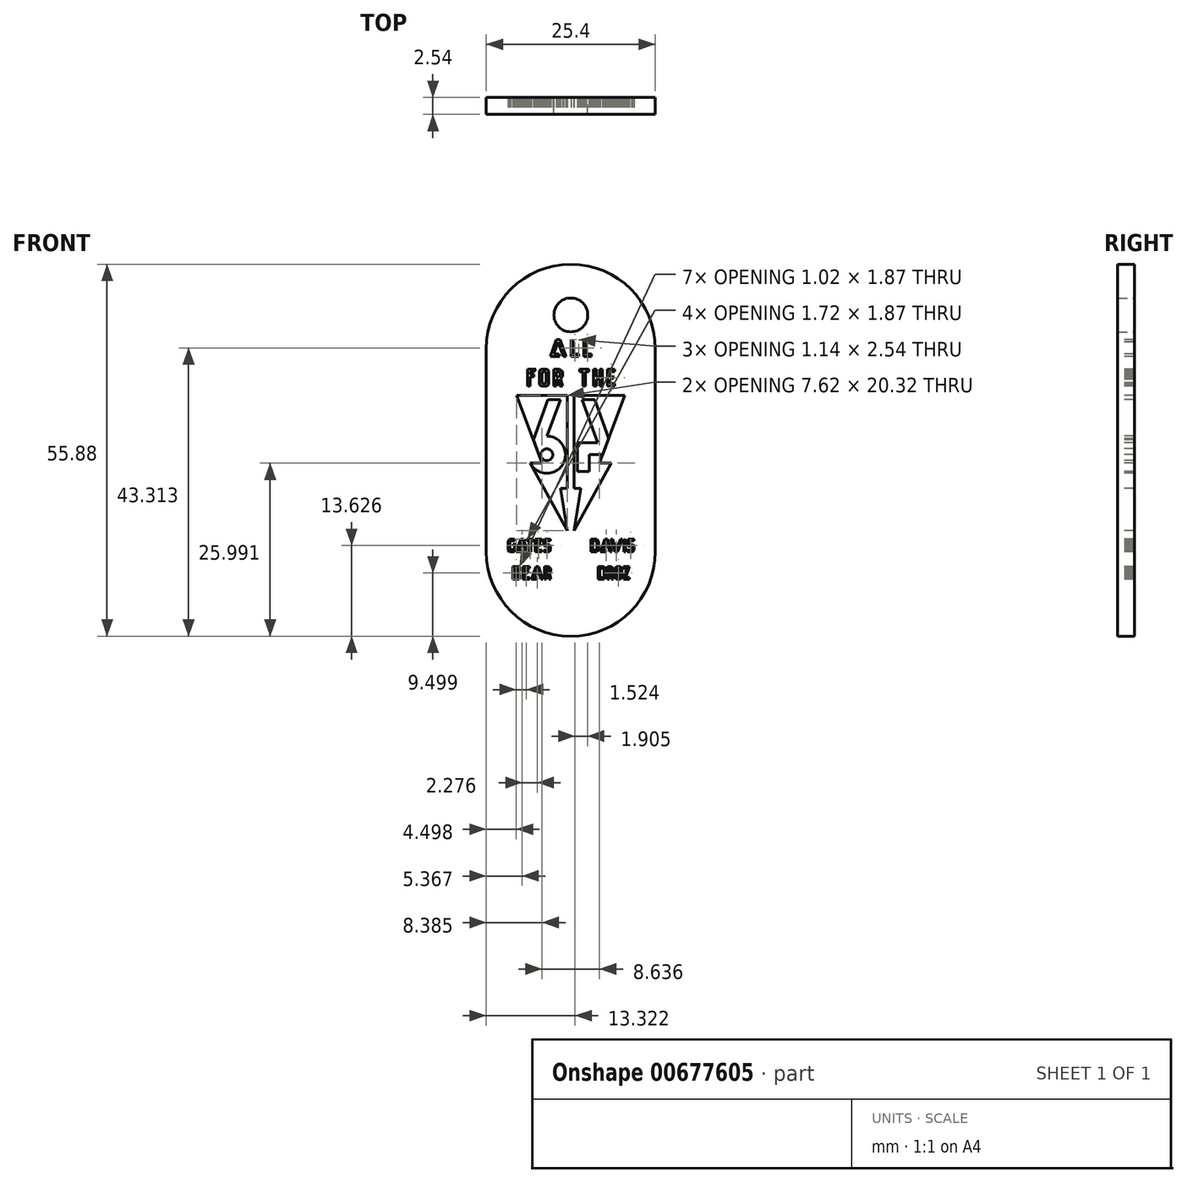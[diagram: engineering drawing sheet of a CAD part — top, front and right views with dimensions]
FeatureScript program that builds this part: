
annotation { "Feature Type Name" : "Feature", "Feature Type Description" : "" }
export const myFeature = defineFeature(function(context is Context, id is Id, definition is map)
    precondition{}
    {
        {
            var Q0;
            Q0=qCreatedBy(makeId("Front.planeOp"),FACE);
            var sketch = newSketch(context, id + "F0", { "sketchPlane" : qUnion([Q0])});
            skLineSegment(sketch, "E0.bottom", {"start": v(-15.5, -1.83) * mm, "end": v(9.9, -1.83) * mm});
            skLineSegment(sketch, "E0.top", {"start": v(-15.5, -32.3) * mm, "end": v(9.9, -32.3) * mm});
            skLineSegment(sketch, "E0.left", {"start": v(-15.5, -1.83) * mm, "end": v(-15.5, -32.3) * mm});
            skLineSegment(sketch, "E0.right", {"start": v(9.9, -1.83) * mm, "end": v(9.9, -32.3) * mm});
            skArc(sketch, "E1", {"start": v(9.9, -1.83) * mm, "mid": v(-2.8, 10.87) * mm, "end": v(-15.5, -1.83) * mm});
            skArc(sketch, "E2", {"start": v(-15.5, -32.3) * mm, "mid": v(-2.8, -45) * mm, "end": v(9.9, -32.3) * mm});
            skCircle(sketch, "E3", {"center": v(-2.8, 3.25) * mm, "radius": 2.54 * mm});
            skSolve(sketch);
        }
        {
            var Q0;
            Q0=makeQuery(id+"F0.imprint","IMPRINT",FACE,{"disambiguationData":[TD([[makeQuery(id+"F0.imprint","IMPRINT",EDGE,{"derivedFrom":sQuery(id+"F0.wireOp",EDGE,"E0.bottom")}),1.0]])]});
            var Q1;
            Q1=makeQuery(id+"F0.imprint","IMPRINT",FACE,{"disambiguationData":[TD([[makeQuery(id+"F0.imprint","IMPRINT",EDGE,{"derivedFrom":sQuery(id+"F0.wireOp",EDGE,"E0.bottom")}),-1.0]])]});
            var Q2;
            Q2=makeQuery(id+"F0.imprint","IMPRINT",FACE,{"disambiguationData":[TD([[makeQuery(id+"F0.imprint","IMPRINT",EDGE,{"derivedFrom":sQuery(id+"F0.wireOp",EDGE,"E0.top")}),-1.0]])]});
            extrude(context, id + "F1", {"entities" : qUnion([Q0, Q1, Q2]), "depth" : 2.54 * mm, "offsetDistance" : 25.4 * mm});
        }
        {
            var Q0;
            Q0=makeQuery(id+"F1.opExtrude","CAP_FACE",FACE,{"disambiguationData":[OSD([sQuery(id+"F0.wireOp",EDGE,"E0.left"),sQuery(id+"F0.wireOp",EDGE,"E0.right"),sQuery(id+"F0.wireOp",EDGE,"E1"),sQuery(id+"F0.wireOp",EDGE,"E2"),sQuery(id+"F0.wireOp",EDGE,"E3")])],"isStart":false});
            var sketch = newSketch(context, id + "F2", { "sketchPlane" : qUnion([Q0])});
            skLineSegment(sketch, "E4", {"start": v(-3.3, -22.83) * mm, "end": v(-4.32, -22.83) * mm});
            skLineSegment(sketch, "E5", {"start": v(-4.32, -22.83) * mm, "end": v(-3.3, -29.18) * mm});
            skLineSegment(sketch, "E6", {"start": v(-3.3, -29.18) * mm, "end": v(-8.9, -19.02) * mm});
            skLineSegment(sketch, "E7", {"start": v(-8.9, -19.02) * mm, "end": v(-7.12, -19.02) * mm});
            skLineSegment(sketch, "E8", {"start": v(-7.12, -19.02) * mm, "end": v(-10.93, -8.86) * mm});
            skLineSegment(sketch, "E9", {"start": v(-10.93, -8.86) * mm, "end": v(-3.3, -8.86) * mm});
            skLineSegment(sketch, "E10", {"start": v(-3.3, -8.86) * mm, "end": v(-3.3, -22.83) * mm});
            skLineSegment(sketch, "E11", {"start": v(-2.8, -46) * mm, "end": v(-2.8, 11.72) * mm});
            skPoint(sketch, "E11.startSnap0", {"position": v(-2.8, -45) * mm});
            skPoint(sketch, "E11.endSnap0", {"position": v(-2.8, 10.87) * mm});
            skLineSegment(sketch, "E12.MirrorCS", {"start": v(-2.29, -8.86) * mm, "end": v(-2.29, -22.83) * mm});
            skLineSegment(sketch, "E13.MirrorCS", {"start": v(5.33, -8.86) * mm, "end": v(-2.29, -8.86) * mm});
            skLineSegment(sketch, "E14.MirrorCS", {"start": v(1.52, -19.02) * mm, "end": v(5.33, -8.86) * mm});
            skLineSegment(sketch, "E15.MirrorCS", {"start": v(3.3, -19.02) * mm, "end": v(1.52, -19.02) * mm});
            skLineSegment(sketch, "E16.MirrorCS", {"start": v(-2.29, -29.18) * mm, "end": v(3.3, -19.02) * mm});
            skLineSegment(sketch, "E17.MirrorCS", {"start": v(-1.27, -22.83) * mm, "end": v(-2.29, -29.18) * mm});
            skLineSegment(sketch, "E18.MirrorCS", {"start": v(-2.29, -22.83) * mm, "end": v(-1.27, -22.83) * mm});
            skSolve(sketch);
        }
        {
            var Q0;
            Q0=makeQuery(id+"F2.imprint","IMPRINT",FACE,{"disambiguationData":[TD([[makeQuery(id+"F2.imprint","IMPRINT",EDGE,{"derivedFrom":sQuery(id+"F2.wireOp",EDGE,"E4")}),-1.0]])]});
            var Q1;
            Q1=makeQuery(id+"F2.imprint","IMPRINT",FACE,{"disambiguationData":[TD([[makeQuery(id+"F2.imprint","IMPRINT",EDGE,{"derivedFrom":sQuery(id+"F2.wireOp",EDGE,"E12.MirrorCS")}),1.0]])]});
            extrude(context, id + "F3", {"entities" : qUnion([Q0, Q1]), "operationType" : NewBodyOperationType.REMOVE, "oppositeDirection" : true, "depth" : 25.4 * mm, "offsetDistance" : 25.4 * mm});
        }
        {
            var Q0;
            Q0=makeQuery(id+"F1.opExtrude","CAP_FACE",FACE,{"disambiguationData":[OSD([sQuery(id+"F0.wireOp",EDGE,"E0.left"),sQuery(id+"F0.wireOp",EDGE,"E0.right"),sQuery(id+"F0.wireOp",EDGE,"E1"),sQuery(id+"F0.wireOp",EDGE,"E2"),sQuery(id+"F0.wireOp",EDGE,"E3")])],"isStart":false});
            var sketch = newSketch(context, id + "F4", { "sketchPlane" : qUnion([Q0])});
            skLineSegment(sketch, "E19", {"start": v(-1.78, -20.29) * mm, "end": v(-1.78, -15.97) * mm});
            skLineSegment(sketch, "E20", {"start": v(-1.78, -15.97) * mm, "end": v(1.27, -15.97) * mm});
            skLineSegment(sketch, "E21", {"start": v(1.27, -15.97) * mm, "end": v(0.13, -12.85) * mm});
            skLineSegment(sketch, "E22", {"start": v(1.52, -11.47) * mm, "end": v(3.8, -17.75) * mm});
            skLineSegment(sketch, "E23", {"start": v(3.8, -17.75) * mm, "end": v(0, -17.75) * mm});
            skLineSegment(sketch, "E24", {"start": v(0, -17.75) * mm, "end": v(0, -20.29) * mm});
            skLineSegment(sketch, "E25", {"start": v(0, -20.29) * mm, "end": v(-1.78, -20.29) * mm});
            skLineSegment(sketch, "E26", {"start": v(0.13, -12.85) * mm, "end": v(-1.09, -9.5) * mm});
            skLineSegment(sketch, "E27", {"start": v(-1.09, -9.5) * mm, "end": v(0.8, -9.5) * mm});
            skLineSegment(sketch, "E28", {"start": v(0.8, -9.5) * mm, "end": v(1.52, -11.47) * mm});
            skCircle(sketch, "E29", {"center": v(-6.4, -17.75) * mm, "radius": 2.8 * mm});
            skLineSegment(sketch, "E30", {"start": v(-8.67, -16.1) * mm, "end": v(-6.26, -9.5) * mm});
            skLineSegment(sketch, "E31", {"start": v(-6.26, -9.5) * mm, "end": v(-4.37, -9.5) * mm});
            skLineSegment(sketch, "E32", {"start": v(-4.37, -9.5) * mm, "end": v(-6.35, -14.96) * mm});
            skCircle(sketch, "E33", {"center": v(-6.4, -17.75) * mm, "radius": 0.89 * mm});
            skSolve(sketch);
        }
        {
            var Q0;
            {var subQ1=sQuery(id+"F4.wireOp",EDGE,"E31");Q0=makeQuery(id+"F4.imprint","IMPRINT",FACE,{"disambiguationData":[TD([[makeQuery(id+"F4.imprint","IMPRINT",EDGE,{"derivedFrom":subQ1}),-1.0]])]});}
            var Q1;
            Q1=makeQuery(id+"F4.imprint","IMPRINT",FACE,{"disambiguationData":[TD([[makeQuery(id+"F4.imprint","IMPRINT",EDGE,{"derivedFrom":sQuery(id+"F4.wireOp",EDGE,"E33")}),-1.0]])]});
            var Q2;
            Q2=makeQuery(id+"F4.imprint","IMPRINT",FACE,{"disambiguationData":[TD([[makeQuery(id+"F4.imprint","IMPRINT",EDGE,{"derivedFrom":sQuery(id+"F4.wireOp",EDGE,"E19")}),-1.0]])]});
            extrude(context, id + "F5", {"entities" : qUnion([Q0, Q1, Q2]), "oppositeDirection" : true, "depth" : 2.54 * mm, "offsetDistance" : 25.4 * mm});
        }
        {
            var Q0;
            Q0=makeQuery(id+"F1.opExtrude","CAP_FACE",FACE,{"disambiguationData":[OSD([sQuery(id+"F0.wireOp",EDGE,"E0.left"),sQuery(id+"F0.wireOp",EDGE,"E0.right"),sQuery(id+"F0.wireOp",EDGE,"E1"),sQuery(id+"F0.wireOp",EDGE,"E2"),sQuery(id+"F0.wireOp",EDGE,"E3")])],"isStart":false});
            var sketch = newSketch(context, id + "F6", { "sketchPlane" : qUnion([Q0])});
            skLineSegment(sketch, "E34", {"start": v(-5.9, -2.97) * mm, "end": v(-4.97, -0.43) * mm});
            skLineSegment(sketch, "E35", {"start": v(-4.97, -0.43) * mm, "end": v(-4.44, -0.43) * mm});
            skLineSegment(sketch, "E36", {"start": v(-4.44, -0.43) * mm, "end": v(-3.51, -2.97) * mm});
            skLineSegment(sketch, "E37", {"start": v(-3.51, -2.97) * mm, "end": v(-3.92, -2.97) * mm});
            skLineSegment(sketch, "E38", {"start": v(-3.92, -2.97) * mm, "end": v(-4.7, -0.8) * mm});
            skLineSegment(sketch, "E39", {"start": v(-4.7, -0.8) * mm, "end": v(-5.35, -2.59) * mm});
            skLineSegment(sketch, "E40", {"start": v(-5.35, -2.59) * mm, "end": v(-4.6, -2.59) * mm});
            skLineSegment(sketch, "E41", {"start": v(-4.6, -2.59) * mm, "end": v(-4.46, -2.97) * mm});
            skLineSegment(sketch, "E42", {"start": v(-4.46, -2.97) * mm, "end": v(-5.9, -2.97) * mm});
            skLineSegment(sketch, "E43", {"start": v(-2.75, -0.43) * mm, "end": v(-2.75, -2.97) * mm});
            skLineSegment(sketch, "E44", {"start": v(-2.75, -2.97) * mm, "end": v(-1.6, -2.97) * mm});
            skLineSegment(sketch, "E45", {"start": v(-1.6, -2.97) * mm, "end": v(-1.6, -2.59) * mm});
            skLineSegment(sketch, "E46", {"start": v(-1.6, -2.59) * mm, "end": v(-2.37, -2.59) * mm});
            skLineSegment(sketch, "E47", {"start": v(-2.37, -2.59) * mm, "end": v(-2.37, -0.75) * mm});
            skLineSegment(sketch, "E48", {"start": v(-2.37, -0.75) * mm, "end": v(-2.75, -0.43) * mm});
            skLineSegment(sketch, "E49", {"start": v(-0.84, -0.43) * mm, "end": v(-0.84, -2.97) * mm});
            skLineSegment(sketch, "E50", {"start": v(-0.84, -2.97) * mm, "end": v(0.3, -2.97) * mm});
            skLineSegment(sketch, "E51", {"start": v(0.3, -2.97) * mm, "end": v(0.3, -2.59) * mm});
            skLineSegment(sketch, "E52", {"start": v(0.3, -2.59) * mm, "end": v(-0.46, -2.59) * mm});
            skLineSegment(sketch, "E53", {"start": v(-0.46, -2.59) * mm, "end": v(-0.46, -0.75) * mm});
            skLineSegment(sketch, "E54", {"start": v(-0.46, -0.75) * mm, "end": v(-0.84, -0.43) * mm});
            skLineSegment(sketch, "E55", {"start": v(-9.28, -7.41) * mm, "end": v(-9.28, -4.87) * mm});
            skLineSegment(sketch, "E56", {"start": v(-9.28, -4.87) * mm, "end": v(-8.01, -4.87) * mm});
            skLineSegment(sketch, "E57", {"start": v(-8.01, -4.87) * mm, "end": v(-8.33, -5.25) * mm});
            skLineSegment(sketch, "E58", {"start": v(-8.33, -5.25) * mm, "end": v(-8.9, -5.25) * mm});
            skLineSegment(sketch, "E59", {"start": v(-8.9, -5.25) * mm, "end": v(-8.9, -5.63) * mm});
            skLineSegment(sketch, "E60", {"start": v(-8.9, -5.63) * mm, "end": v(-8.33, -5.63) * mm});
            skLineSegment(sketch, "E61", {"start": v(-8.33, -5.63) * mm, "end": v(-8.33, -6.01) * mm});
            skLineSegment(sketch, "E62", {"start": v(-8.33, -6.01) * mm, "end": v(-8.9, -6.01) * mm});
            skLineSegment(sketch, "E63", {"start": v(-8.9, -6.01) * mm, "end": v(-8.9, -7.41) * mm});
            skLineSegment(sketch, "E64", {"start": v(-8.9, -7.41) * mm, "end": v(-9.28, -7.41) * mm});
            skLineSegment(sketch, "E65", {"start": v(-7.25, -4.87) * mm, "end": v(-7.5, -5.13) * mm});
            skLineSegment(sketch, "E66", {"start": v(-7.5, -5.13) * mm, "end": v(-7.5, -7.16) * mm});
            skLineSegment(sketch, "E67", {"start": v(-7.5, -7.16) * mm, "end": v(-7.25, -7.41) * mm});
            skLineSegment(sketch, "E68", {"start": v(-7.25, -7.41) * mm, "end": v(-6.36, -7.41) * mm});
            skLineSegment(sketch, "E69", {"start": v(-6.36, -7.41) * mm, "end": v(-6.1, -7.16) * mm});
            skLineSegment(sketch, "E70", {"start": v(-6.1, -7.16) * mm, "end": v(-6.1, -5.13) * mm});
            skLineSegment(sketch, "E71", {"start": v(-6.1, -5.13) * mm, "end": v(-6.36, -4.87) * mm});
            skLineSegment(sketch, "E72", {"start": v(-6.36, -4.87) * mm, "end": v(-7.25, -4.87) * mm});
            skLineSegment(sketch, "E73", {"start": v(-5.34, -7.41) * mm, "end": v(-5.34, -4.87) * mm});
            skLineSegment(sketch, "E74", {"start": v(-5.34, -4.87) * mm, "end": v(-4.47, -4.87) * mm});
            skLineSegment(sketch, "E75", {"start": v(-4.47, -4.87) * mm, "end": v(-4.06, -5.29) * mm});
            skLineSegment(sketch, "E76", {"start": v(-4.06, -5.29) * mm, "end": v(-4.06, -5.98) * mm});
            skLineSegment(sketch, "E77", {"start": v(-4.06, -5.98) * mm, "end": v(-4.35, -6.27) * mm});
            skLineSegment(sketch, "E78", {"start": v(-4.35, -6.27) * mm, "end": v(-4.06, -7.41) * mm});
            skLineSegment(sketch, "E79", {"start": v(-4.06, -7.41) * mm, "end": v(-4.45, -7.41) * mm});
            skLineSegment(sketch, "E80", {"start": v(-4.45, -7.41) * mm, "end": v(-4.7, -6.4) * mm});
            skLineSegment(sketch, "E81", {"start": v(-4.7, -6.4) * mm, "end": v(-4.96, -6.4) * mm});
            skLineSegment(sketch, "E82", {"start": v(-4.96, -6.4) * mm, "end": v(-4.96, -7.41) * mm});
            skLineSegment(sketch, "E83", {"start": v(-4.96, -7.41) * mm, "end": v(-5.34, -7.41) * mm});
            skLineSegment(sketch, "E84", {"start": v(-7.12, -6.9) * mm, "end": v(-7, -7.03) * mm});
            skLineSegment(sketch, "E85", {"start": v(-7, -7.03) * mm, "end": v(-6.61, -7.03) * mm});
            skLineSegment(sketch, "E86", {"start": v(-6.61, -7.03) * mm, "end": v(-6.49, -6.9) * mm});
            skLineSegment(sketch, "E87", {"start": v(-6.49, -6.9) * mm, "end": v(-6.49, -5.38) * mm});
            skLineSegment(sketch, "E88", {"start": v(-6.49, -5.38) * mm, "end": v(-6.61, -5.25) * mm});
            skLineSegment(sketch, "E89", {"start": v(-6.61, -5.25) * mm, "end": v(-7, -5.25) * mm});
            skLineSegment(sketch, "E90", {"start": v(-7, -5.25) * mm, "end": v(-7.12, -5.38) * mm});
            skLineSegment(sketch, "E91", {"start": v(-7.12, -5.38) * mm, "end": v(-7.12, -6.9) * mm});
            skLineSegment(sketch, "E92", {"start": v(-4.96, -5.25) * mm, "end": v(-4.96, -6.01) * mm});
            skLineSegment(sketch, "E93", {"start": v(-4.96, -6.01) * mm, "end": v(-4.63, -6.01) * mm});
            skLineSegment(sketch, "E94", {"start": v(-4.63, -6.01) * mm, "end": v(-4.44, -5.82) * mm});
            skLineSegment(sketch, "E95", {"start": v(-4.44, -5.82) * mm, "end": v(-4.44, -5.44) * mm});
            skLineSegment(sketch, "E96", {"start": v(-4.44, -5.44) * mm, "end": v(-4.63, -5.25) * mm});
            skLineSegment(sketch, "E97", {"start": v(-4.63, -5.25) * mm, "end": v(-4.96, -5.25) * mm});
            skLineSegment(sketch, "E98", {"start": v(-1.52, -4.87) * mm, "end": v(-1.52, -5.25) * mm});
            skLineSegment(sketch, "E99", {"start": v(-1.52, -5.25) * mm, "end": v(-1.01, -5.25) * mm});
            skLineSegment(sketch, "E100", {"start": v(-1.01, -5.25) * mm, "end": v(-1.01, -7.41) * mm});
            skLineSegment(sketch, "E101", {"start": v(-1.01, -7.41) * mm, "end": v(-0.63, -7.41) * mm});
            skLineSegment(sketch, "E102", {"start": v(-0.63, -7.41) * mm, "end": v(-0.63, -5.25) * mm});
            skLineSegment(sketch, "E103", {"start": v(-0.63, -5.25) * mm, "end": v(-0.12, -5.25) * mm});
            skLineSegment(sketch, "E104", {"start": v(-0.12, -5.25) * mm, "end": v(-0.12, -4.87) * mm});
            skLineSegment(sketch, "E105", {"start": v(-1.52, -4.87) * mm, "end": v(-0.12, -4.87) * mm});
            skLineSegment(sketch, "E106", {"start": v(0.64, -4.87) * mm, "end": v(0.64, -7.41) * mm});
            skLineSegment(sketch, "E107", {"start": v(0.64, -7.41) * mm, "end": v(1.02, -7.41) * mm});
            skLineSegment(sketch, "E108", {"start": v(1.02, -7.41) * mm, "end": v(1.02, -6.4) * mm});
            skLineSegment(sketch, "E109", {"start": v(1.02, -6.4) * mm, "end": v(1.53, -6.4) * mm});
            skLineSegment(sketch, "E110", {"start": v(1.53, -6.4) * mm, "end": v(1.53, -7.41) * mm});
            skLineSegment(sketch, "E111", {"start": v(1.53, -7.41) * mm, "end": v(1.9, -7.41) * mm});
            skLineSegment(sketch, "E112", {"start": v(1.9, -7.41) * mm, "end": v(1.9, -4.87) * mm});
            skLineSegment(sketch, "E113", {"start": v(1.9, -4.87) * mm, "end": v(1.53, -4.87) * mm});
            skLineSegment(sketch, "E114", {"start": v(1.53, -4.87) * mm, "end": v(1.53, -6.01) * mm});
            skLineSegment(sketch, "E115", {"start": v(1.53, -6.01) * mm, "end": v(1.02, -6.01) * mm});
            skLineSegment(sketch, "E116", {"start": v(1.02, -6.01) * mm, "end": v(1.02, -4.87) * mm});
            skLineSegment(sketch, "E117", {"start": v(1.02, -4.87) * mm, "end": v(0.64, -4.87) * mm});
            skLineSegment(sketch, "E118", {"start": v(2.67, -4.87) * mm, "end": v(2.67, -7.41) * mm});
            skLineSegment(sketch, "E119", {"start": v(2.67, -7.41) * mm, "end": v(3.81, -7.41) * mm});
            skLineSegment(sketch, "E120", {"start": v(3.81, -7.41) * mm, "end": v(3.81, -7.03) * mm});
            skLineSegment(sketch, "E121", {"start": v(3.81, -7.03) * mm, "end": v(3.05, -7.03) * mm});
            skLineSegment(sketch, "E122", {"start": v(3.05, -7.03) * mm, "end": v(3.05, -6.4) * mm});
            skLineSegment(sketch, "E123", {"start": v(3.05, -6.4) * mm, "end": v(3.37, -6.4) * mm});
            skLineSegment(sketch, "E124", {"start": v(3.37, -6.4) * mm, "end": v(3.69, -6.01) * mm});
            skLineSegment(sketch, "E125", {"start": v(3.69, -6.01) * mm, "end": v(3.05, -6.01) * mm});
            skLineSegment(sketch, "E126", {"start": v(3.05, -6.01) * mm, "end": v(3.05, -5.25) * mm});
            skLineSegment(sketch, "E127", {"start": v(3.05, -5.25) * mm, "end": v(3.81, -5.25) * mm});
            skLineSegment(sketch, "E128", {"start": v(3.81, -5.25) * mm, "end": v(3.81, -4.87) * mm});
            skLineSegment(sketch, "E129", {"start": v(3.81, -4.87) * mm, "end": v(2.67, -4.87) * mm});
            skSolve(sketch);
        }
        {
            var Q0;
            Q0=makeQuery(id+"F6.imprint","IMPRINT",FACE,{"disambiguationData":[TD([[makeQuery(id+"F6.imprint","IMPRINT",EDGE,{"derivedFrom":sQuery(id+"F6.wireOp",EDGE,"E34")}),-1.0]])]});
            var Q1;
            Q1=makeQuery(id+"F6.imprint","IMPRINT",FACE,{"disambiguationData":[TD([[makeQuery(id+"F6.imprint","IMPRINT",EDGE,{"derivedFrom":sQuery(id+"F6.wireOp",EDGE,"E43")}),1.0]])]});
            var Q2;
            Q2=makeQuery(id+"F6.imprint","IMPRINT",FACE,{"disambiguationData":[TD([[makeQuery(id+"F6.imprint","IMPRINT",EDGE,{"derivedFrom":sQuery(id+"F6.wireOp",EDGE,"E49")}),1.0]])]});
            var Q3;
            Q3=makeQuery(id+"F6.imprint","IMPRINT",FACE,{"disambiguationData":[TD([[makeQuery(id+"F6.imprint","IMPRINT",EDGE,{"derivedFrom":sQuery(id+"F6.wireOp",EDGE,"9PJnOvU5-sTbl-nWi6-ZAvp-PHSVYoyPzlgs")}),-1.0]])]});
            var Q4;
            Q4=makeQuery(id+"F6.imprint","IMPRINT",FACE,{"disambiguationData":[TD([[makeQuery(id+"F6.imprint","IMPRINT",EDGE,{"derivedFrom":sQuery(id+"F6.wireOp",EDGE,"RmkwvY6V-nyv5-Yecy-RsY6-h2SH7d8XhEEe")}),-1.0]])]});
            var Q5;
            Q5=makeQuery(id+"F6.imprint","IMPRINT",FACE,{"disambiguationData":[TD([[makeQuery(id+"F6.imprint","IMPRINT",EDGE,{"derivedFrom":sQuery(id+"F6.wireOp",EDGE,"E55")}),-1.0]])]});
            var Q6;
            Q6=makeQuery(id+"F6.imprint","IMPRINT",FACE,{"disambiguationData":[TD([[makeQuery(id+"F6.imprint","IMPRINT",EDGE,{"derivedFrom":sQuery(id+"F6.wireOp",EDGE,"E65")}),1.0]])]});
            var Q7;
            Q7=makeQuery(id+"F6.imprint","IMPRINT",FACE,{"disambiguationData":[TD([[makeQuery(id+"F6.imprint","IMPRINT",EDGE,{"derivedFrom":sQuery(id+"F6.wireOp",EDGE,"E73")}),-1.0]])]});
            var Q8;
            Q8=makeQuery(id+"F6.imprint","IMPRINT",FACE,{"disambiguationData":[TD([[makeQuery(id+"F6.imprint","IMPRINT",EDGE,{"derivedFrom":sQuery(id+"F6.wireOp",EDGE,"E98")}),1.0]])]});
            var Q9;
            Q9=makeQuery(id+"F6.imprint","IMPRINT",FACE,{"disambiguationData":[TD([[makeQuery(id+"F6.imprint","IMPRINT",EDGE,{"derivedFrom":sQuery(id+"F6.wireOp",EDGE,"E106")}),1.0]])]});
            var Q10;
            Q10=makeQuery(id+"F6.imprint","IMPRINT",FACE,{"disambiguationData":[TD([[makeQuery(id+"F6.imprint","IMPRINT",EDGE,{"derivedFrom":sQuery(id+"F6.wireOp",EDGE,"E118")}),1.0]])]});
            extrude(context, id + "F7", {"entities" : qUnion([Q0, Q1, Q2, Q3, Q4, Q5, Q6, Q7, Q8, Q9, Q10]), "operationType" : NewBodyOperationType.REMOVE, "oppositeDirection" : true, "depth" : 25.4 * mm, "offsetDistance" : 25.4 * mm});
        }
        {
            var Q0;
            {var subQ0=sQuery(id+"F0.wireOp",EDGE,"E0.left");var subQ1=sQuery(id+"F0.wireOp",EDGE,"E1");var subQ2=sQuery(id+"F0.wireOp",EDGE,"E0.right");var subQ3=sQuery(id+"F0.wireOp",EDGE,"E2");var subQ4=sQuery(id+"F0.wireOp",EDGE,"E3");Q0=makeQuery(id+"F7.boolean.opBoolean","SPLIT",FACE,{"disambiguationData":[TD([makeQuery(id+"F1.opExtrude","SWEPT_FACE",FACE,{"disambiguationData":[OSD([subQ0])]})])],"derivedFrom":makeQuery(id+"F1.opExtrude","CAP_FACE",FACE,{"disambiguationData":[OSD([subQ0,subQ2,subQ1,subQ3,subQ4])],"isStart":false})});}
            var sketch = newSketch(context, id + "F8", { "sketchPlane" : qUnion([Q0])});
            skLineSegment(sketch, "E130", {"start": v(-12.2, -30.78) * mm, "end": v(-12.2, -31.99) * mm});
            skLineSegment(sketch, "E131", {"start": v(-12.2, -31.99) * mm, "end": v(-12, -32.32) * mm});
            skLineSegment(sketch, "E132", {"start": v(-12, -32.32) * mm, "end": v(-11.25, -32.32) * mm});
            skLineSegment(sketch, "E133", {"start": v(-11.25, -32.32) * mm, "end": v(-11.01, -31.91) * mm});
            skLineSegment(sketch, "E134", {"start": v(-11.01, -31.91) * mm, "end": v(-11.01, -31.21) * mm});
            skLineSegment(sketch, "E135", {"start": v(-11.01, -31.21) * mm, "end": v(-11.44, -31.21) * mm});
            skLineSegment(sketch, "E136", {"start": v(-11.44, -31.21) * mm, "end": v(-11.44, -31.46) * mm});
            skLineSegment(sketch, "E137", {"start": v(-11.44, -31.46) * mm, "end": v(-11.27, -31.46) * mm});
            skLineSegment(sketch, "E138", {"start": v(-11.27, -31.46) * mm, "end": v(-11.27, -31.85) * mm});
            skLineSegment(sketch, "E139", {"start": v(-11.27, -31.85) * mm, "end": v(-11.37, -32.02) * mm});
            skLineSegment(sketch, "E140", {"start": v(-11.37, -32.02) * mm, "end": v(-11.84, -32.02) * mm});
            skLineSegment(sketch, "E141", {"start": v(-11.84, -32.02) * mm, "end": v(-11.94, -31.85) * mm});
            skLineSegment(sketch, "E142", {"start": v(-11.94, -31.85) * mm, "end": v(-11.94, -30.88) * mm});
            skLineSegment(sketch, "E143", {"start": v(-11.94, -30.88) * mm, "end": v(-11.84, -30.7) * mm});
            skLineSegment(sketch, "E144", {"start": v(-11.84, -30.7) * mm, "end": v(-11.27, -30.7) * mm});
            skLineSegment(sketch, "E145", {"start": v(-11.27, -30.7) * mm, "end": v(-11.27, -30.45) * mm});
            skLineSegment(sketch, "E146", {"start": v(-11.27, -30.45) * mm, "end": v(-12, -30.45) * mm});
            skLineSegment(sketch, "E147", {"start": v(-12, -30.45) * mm, "end": v(-12.2, -30.78) * mm});
            skLineSegment(sketch, "E148", {"start": v(-11, -32.32) * mm, "end": v(-10.31, -30.45) * mm});
            skLineSegment(sketch, "E149", {"start": v(-9.95, -30.45) * mm, "end": v(-9.27, -32.32) * mm});
            skLineSegment(sketch, "E150", {"start": v(-9.27, -32.32) * mm, "end": v(-9.54, -32.32) * mm});
            skLineSegment(sketch, "E151", {"start": v(-9.54, -32.32) * mm, "end": v(-10.13, -30.7) * mm});
            skLineSegment(sketch, "E152", {"start": v(-10.13, -30.7) * mm, "end": v(-10.63, -32.06) * mm});
            skLineSegment(sketch, "E153", {"start": v(-10.63, -32.06) * mm, "end": v(-10.25, -32.06) * mm});
            skLineSegment(sketch, "E154", {"start": v(-10.25, -32.06) * mm, "end": v(-10.1, -32.32) * mm});
            skLineSegment(sketch, "E155", {"start": v(-10.1, -32.32) * mm, "end": v(-11, -32.32) * mm});
            skLineSegment(sketch, "E156", {"start": v(-10.31, -30.45) * mm, "end": v(-9.95, -30.45) * mm});
            skLineSegment(sketch, "E157", {"start": v(-9.4, -30.45) * mm, "end": v(-8.39, -30.45) * mm});
            skLineSegment(sketch, "E158", {"start": v(-8.39, -30.45) * mm, "end": v(-8.39, -30.7) * mm});
            skLineSegment(sketch, "E159", {"start": v(-8.39, -30.7) * mm, "end": v(-8.77, -30.7) * mm});
            skLineSegment(sketch, "E160", {"start": v(-8.77, -30.7) * mm, "end": v(-8.77, -32.32) * mm});
            skLineSegment(sketch, "E161", {"start": v(-8.77, -32.32) * mm, "end": v(-9.02, -32.32) * mm});
            skLineSegment(sketch, "E162", {"start": v(-9.02, -32.32) * mm, "end": v(-9.02, -30.7) * mm});
            skLineSegment(sketch, "E163", {"start": v(-9.02, -30.7) * mm, "end": v(-9.4, -30.7) * mm});
            skLineSegment(sketch, "E164", {"start": v(-9.4, -30.7) * mm, "end": v(-9.4, -30.45) * mm});
            skLineSegment(sketch, "E165", {"start": v(-8.13, -32.32) * mm, "end": v(-7.12, -32.32) * mm});
            skLineSegment(sketch, "E166", {"start": v(-7.12, -32.32) * mm, "end": v(-7.12, -32.06) * mm});
            skLineSegment(sketch, "E167", {"start": v(-7.12, -32.06) * mm, "end": v(-7.88, -32.06) * mm});
            skLineSegment(sketch, "E168", {"start": v(-7.88, -32.06) * mm, "end": v(-7.88, -31.4) * mm});
            skLineSegment(sketch, "E169", {"start": v(-7.88, -31.4) * mm, "end": v(-7.39, -31.4) * mm});
            skLineSegment(sketch, "E170", {"start": v(-7.39, -31.4) * mm, "end": v(-7.24, -31.15) * mm});
            skLineSegment(sketch, "E171", {"start": v(-7.24, -31.15) * mm, "end": v(-7.88, -31.15) * mm});
            skLineSegment(sketch, "E172", {"start": v(-7.12, -30.45) * mm, "end": v(-8.13, -30.45) * mm});
            skLineSegment(sketch, "E173", {"start": v(-5.85, -30.45) * mm, "end": v(-6.7, -30.45) * mm});
            skLineSegment(sketch, "E174", {"start": v(-6.7, -30.45) * mm, "end": v(-6.86, -30.72) * mm});
            skLineSegment(sketch, "E175", {"start": v(-6.86, -30.72) * mm, "end": v(-6.86, -31.23) * mm});
            skLineSegment(sketch, "E176", {"start": v(-6.86, -31.23) * mm, "end": v(-6.7, -31.5) * mm});
            skLineSegment(sketch, "E177", {"start": v(-6.7, -31.5) * mm, "end": v(-6.2, -31.5) * mm});
            skLineSegment(sketch, "E178", {"start": v(-6.2, -31.5) * mm, "end": v(-6.1, -31.68) * mm});
            skLineSegment(sketch, "E179", {"start": v(-6.1, -31.68) * mm, "end": v(-6.1, -31.89) * mm});
            skLineSegment(sketch, "E180", {"start": v(-6.1, -31.89) * mm, "end": v(-6.2, -32.06) * mm});
            skLineSegment(sketch, "E181", {"start": v(-6.2, -32.06) * mm, "end": v(-6.86, -32.06) * mm});
            skLineSegment(sketch, "E182", {"start": v(-6.86, -32.32) * mm, "end": v(-6, -32.32) * mm});
            skLineSegment(sketch, "E183", {"start": v(-6, -32.32) * mm, "end": v(-5.85, -32.06) * mm});
            skLineSegment(sketch, "E184", {"start": v(-5.85, -32.06) * mm, "end": v(-5.85, -31.56) * mm});
            skLineSegment(sketch, "E185", {"start": v(-5.85, -31.56) * mm, "end": v(-6.02, -31.25) * mm});
            skLineSegment(sketch, "E186", {"start": v(-6.02, -31.25) * mm, "end": v(-6.5, -31.25) * mm});
            skLineSegment(sketch, "E187", {"start": v(-6.5, -30.7) * mm, "end": v(-5.85, -30.7) * mm});
            skLineSegment(sketch, "E188", {"start": v(-5.85, -30.7) * mm, "end": v(-5.85, -30.45) * mm});
            skLineSegment(sketch, "E189", {"start": v(-8.13, -30.45) * mm, "end": v(-8.13, -32.32) * mm});
            skLineSegment(sketch, "E190", {"start": v(-6.86, -32.06) * mm, "end": v(-6.86, -32.32) * mm});
            skLineSegment(sketch, "E191", {"start": v(-6.5, -30.7) * mm, "end": v(-6.6, -30.88) * mm});
            skLineSegment(sketch, "E192", {"start": v(-6.6, -30.88) * mm, "end": v(-6.6, -31.08) * mm});
            skLineSegment(sketch, "E193", {"start": v(-6.6, -31.08) * mm, "end": v(-6.5, -31.25) * mm});
            skLineSegment(sketch, "E194", {"start": v(-7.88, -31.15) * mm, "end": v(-7.88, -30.7) * mm});
            skLineSegment(sketch, "E195", {"start": v(-7.88, -30.7) * mm, "end": v(-7.12, -30.7) * mm});
            skLineSegment(sketch, "E196", {"start": v(-7.12, -30.7) * mm, "end": v(-7.12, -30.45) * mm});
            skLineSegment(sketch, "E197", {"start": v(0.25, -30.45) * mm, "end": v(0.25, -32.32) * mm});
            skLineSegment(sketch, "E198", {"start": v(0.25, -32.32) * mm, "end": v(1.14, -32.32) * mm});
            skLineSegment(sketch, "E199", {"start": v(1.14, -32.32) * mm, "end": v(1.4, -31.88) * mm});
            skLineSegment(sketch, "E200", {"start": v(1.4, -31.88) * mm, "end": v(1.4, -30.89) * mm});
            skLineSegment(sketch, "E201", {"start": v(1.4, -30.89) * mm, "end": v(1.14, -30.45) * mm});
            skLineSegment(sketch, "E202", {"start": v(1.14, -30.45) * mm, "end": v(0.25, -30.45) * mm});
            skLineSegment(sketch, "E203", {"start": v(1.65, -32.32) * mm, "end": v(2.33, -30.45) * mm});
            skLineSegment(sketch, "E204", {"start": v(2.33, -30.45) * mm, "end": v(2.68, -30.45) * mm});
            skLineSegment(sketch, "E205", {"start": v(2.68, -30.45) * mm, "end": v(3.36, -32.32) * mm});
            skLineSegment(sketch, "E206", {"start": v(3.36, -32.32) * mm, "end": v(3.1, -32.32) * mm});
            skLineSegment(sketch, "E207", {"start": v(3.1, -32.32) * mm, "end": v(2.5, -30.7) * mm});
            skLineSegment(sketch, "E208", {"start": v(2.5, -30.7) * mm, "end": v(2.01, -32.06) * mm});
            skLineSegment(sketch, "E209", {"start": v(2.01, -32.06) * mm, "end": v(2.4, -32.06) * mm});
            skLineSegment(sketch, "E210", {"start": v(2.4, -32.06) * mm, "end": v(2.54, -32.32) * mm});
            skLineSegment(sketch, "E211", {"start": v(2.54, -32.32) * mm, "end": v(1.65, -32.32) * mm});
            skLineSegment(sketch, "E212", {"start": v(0.5, -30.7) * mm, "end": v(0.5, -32.06) * mm});
            skLineSegment(sketch, "E213", {"start": v(0.5, -32.06) * mm, "end": v(1, -32.06) * mm});
            skLineSegment(sketch, "E214", {"start": v(1, -32.06) * mm, "end": v(1.14, -31.81) * mm});
            skLineSegment(sketch, "E215", {"start": v(1.14, -31.81) * mm, "end": v(1.14, -30.96) * mm});
            skLineSegment(sketch, "E216", {"start": v(1.14, -30.96) * mm, "end": v(1, -30.7) * mm});
            skLineSegment(sketch, "E217", {"start": v(1, -30.7) * mm, "end": v(0.5, -30.7) * mm});
            skLineSegment(sketch, "E218", {"start": v(3.2, -30.45) * mm, "end": v(3.87, -32.32) * mm});
            skLineSegment(sketch, "E219", {"start": v(3.87, -32.32) * mm, "end": v(4.23, -32.32) * mm});
            skLineSegment(sketch, "E220", {"start": v(4.23, -32.32) * mm, "end": v(4.9, -30.45) * mm});
            skLineSegment(sketch, "E221", {"start": v(4.9, -30.45) * mm, "end": v(4.64, -30.45) * mm});
            skLineSegment(sketch, "E222", {"start": v(4.64, -30.45) * mm, "end": v(4.05, -32.06) * mm});
            skLineSegment(sketch, "E223", {"start": v(4.05, -32.06) * mm, "end": v(3.46, -30.45) * mm});
            skLineSegment(sketch, "E224", {"start": v(3.46, -30.45) * mm, "end": v(3.2, -30.45) * mm});
            skLineSegment(sketch, "E225", {"start": v(5.16, -30.45) * mm, "end": v(5.16, -32.32) * mm});
            skLineSegment(sketch, "E226", {"start": v(5.16, -32.32) * mm, "end": v(5.42, -32.32) * mm});
            skLineSegment(sketch, "E227", {"start": v(5.42, -32.32) * mm, "end": v(5.42, -30.6) * mm});
            skLineSegment(sketch, "E228", {"start": v(5.42, -30.6) * mm, "end": v(5.16, -30.45) * mm});
            skLineSegment(sketch, "E229", {"start": v(6.69, -30.45) * mm, "end": v(5.83, -30.45) * mm});
            skLineSegment(sketch, "E230", {"start": v(5.83, -30.45) * mm, "end": v(5.67, -30.72) * mm});
            skLineSegment(sketch, "E231", {"start": v(5.67, -30.72) * mm, "end": v(5.67, -31.23) * mm});
            skLineSegment(sketch, "E232", {"start": v(5.67, -31.23) * mm, "end": v(5.83, -31.5) * mm});
            skLineSegment(sketch, "E233", {"start": v(5.83, -31.5) * mm, "end": v(6.33, -31.5) * mm});
            skLineSegment(sketch, "E234", {"start": v(6.33, -31.5) * mm, "end": v(6.43, -31.68) * mm});
            skLineSegment(sketch, "E235", {"start": v(6.43, -31.68) * mm, "end": v(6.43, -31.89) * mm});
            skLineSegment(sketch, "E236", {"start": v(6.43, -31.89) * mm, "end": v(6.33, -32.06) * mm});
            skLineSegment(sketch, "E237", {"start": v(6.33, -32.06) * mm, "end": v(5.67, -32.06) * mm});
            skLineSegment(sketch, "E238", {"start": v(5.67, -32.32) * mm, "end": v(6.54, -32.32) * mm});
            skLineSegment(sketch, "E239", {"start": v(6.54, -32.32) * mm, "end": v(6.69, -32.06) * mm});
            skLineSegment(sketch, "E240", {"start": v(6.69, -32.06) * mm, "end": v(6.69, -31.56) * mm});
            skLineSegment(sketch, "E241", {"start": v(6.69, -31.56) * mm, "end": v(6.51, -31.25) * mm});
            skLineSegment(sketch, "E242", {"start": v(6.51, -31.25) * mm, "end": v(6.03, -31.25) * mm});
            skLineSegment(sketch, "E243", {"start": v(6.03, -30.7) * mm, "end": v(6.69, -30.7) * mm});
            skLineSegment(sketch, "E244", {"start": v(6.69, -30.7) * mm, "end": v(6.69, -30.45) * mm});
            skLineSegment(sketch, "E245", {"start": v(5.67, -32.06) * mm, "end": v(5.67, -32.32) * mm});
            skLineSegment(sketch, "E246", {"start": v(6.03, -30.7) * mm, "end": v(5.93, -30.88) * mm});
            skLineSegment(sketch, "E247", {"start": v(5.93, -30.88) * mm, "end": v(5.93, -31.08) * mm});
            skLineSegment(sketch, "E248", {"start": v(5.93, -31.08) * mm, "end": v(6.03, -31.25) * mm});
            skLineSegment(sketch, "E249", {"start": v(-11.5, -34.58) * mm, "end": v(-11.5, -36.45) * mm});
            skLineSegment(sketch, "E250", {"start": v(-11.5, -36.45) * mm, "end": v(-10.58, -36.45) * mm});
            skLineSegment(sketch, "E251", {"start": v(-10.58, -36.45) * mm, "end": v(-10.5, -36.3) * mm});
            skLineSegment(sketch, "E252", {"start": v(-10.5, -36.3) * mm, "end": v(-10.5, -35.8) * mm});
            skLineSegment(sketch, "E253", {"start": v(-10.5, -35.23) * mm, "end": v(-10.5, -34.72) * mm});
            skLineSegment(sketch, "E254", {"start": v(-10.5, -34.72) * mm, "end": v(-10.58, -34.58) * mm});
            skLineSegment(sketch, "E255", {"start": v(-10.58, -34.58) * mm, "end": v(-11.5, -34.58) * mm});
            skLineSegment(sketch, "E256", {"start": v(-10.5, -35.23) * mm, "end": v(-10.62, -35.45) * mm});
            skLineSegment(sketch, "E257", {"start": v(-10.62, -35.45) * mm, "end": v(-10.62, -35.57) * mm});
            skLineSegment(sketch, "E258", {"start": v(-10.62, -35.57) * mm, "end": v(-10.5, -35.8) * mm});
            skLineSegment(sketch, "E259", {"start": v(-11.26, -34.83) * mm, "end": v(-11.26, -35.43) * mm});
            skLineSegment(sketch, "E260", {"start": v(-11.26, -35.43) * mm, "end": v(-10.87, -35.43) * mm});
            skLineSegment(sketch, "E261", {"start": v(-10.87, -35.43) * mm, "end": v(-10.75, -35.21) * mm});
            skLineSegment(sketch, "E262", {"start": v(-10.75, -35.21) * mm, "end": v(-10.75, -35.05) * mm});
            skLineSegment(sketch, "E263", {"start": v(-10.75, -35.05) * mm, "end": v(-10.87, -34.83) * mm});
            skLineSegment(sketch, "E264", {"start": v(-10.87, -34.83) * mm, "end": v(-11.26, -34.83) * mm});
            skLineSegment(sketch, "E265", {"start": v(-11.26, -35.56) * mm, "end": v(-10.87, -35.56) * mm});
            skLineSegment(sketch, "E266", {"start": v(-10.87, -35.56) * mm, "end": v(-10.75, -35.78) * mm});
            skLineSegment(sketch, "E267", {"start": v(-10.75, -35.78) * mm, "end": v(-10.75, -35.97) * mm});
            skLineSegment(sketch, "E268", {"start": v(-10.75, -35.97) * mm, "end": v(-10.87, -36.2) * mm});
            skLineSegment(sketch, "E269", {"start": v(-10.87, -36.2) * mm, "end": v(-11.26, -36.2) * mm});
            skLineSegment(sketch, "E270", {"start": v(-11.26, -36.2) * mm, "end": v(-11.26, -35.56) * mm});
            skLineSegment(sketch, "E271", {"start": v(-9.99, -36.45) * mm, "end": v(-8.97, -36.45) * mm});
            skLineSegment(sketch, "E272", {"start": v(-8.97, -36.45) * mm, "end": v(-8.97, -36.2) * mm});
            skLineSegment(sketch, "E273", {"start": v(-8.97, -36.2) * mm, "end": v(-9.73, -36.2) * mm});
            skLineSegment(sketch, "E274", {"start": v(-9.73, -36.2) * mm, "end": v(-9.73, -35.53) * mm});
            skLineSegment(sketch, "E275", {"start": v(-9.73, -35.53) * mm, "end": v(-9.24, -35.53) * mm});
            skLineSegment(sketch, "E276", {"start": v(-9.24, -35.53) * mm, "end": v(-9.1, -35.28) * mm});
            skLineSegment(sketch, "E277", {"start": v(-9.1, -35.28) * mm, "end": v(-9.73, -35.28) * mm});
            skLineSegment(sketch, "E278", {"start": v(-8.97, -34.58) * mm, "end": v(-9.99, -34.58) * mm});
            skLineSegment(sketch, "E279", {"start": v(-9.99, -34.58) * mm, "end": v(-9.99, -36.45) * mm});
            skLineSegment(sketch, "E280", {"start": v(-9.73, -35.28) * mm, "end": v(-9.73, -34.83) * mm});
            skLineSegment(sketch, "E281", {"start": v(-9.73, -34.83) * mm, "end": v(-8.97, -34.83) * mm});
            skLineSegment(sketch, "E282", {"start": v(-8.97, -34.83) * mm, "end": v(-8.97, -34.58) * mm});
            skLineSegment(sketch, "E283", {"start": v(-8.72, -36.45) * mm, "end": v(-8.03, -34.58) * mm});
            skLineSegment(sketch, "E284", {"start": v(-7.68, -34.58) * mm, "end": v(-7, -36.45) * mm});
            skLineSegment(sketch, "E285", {"start": v(-7, -36.45) * mm, "end": v(-7.27, -36.45) * mm});
            skLineSegment(sketch, "E286", {"start": v(-7.27, -36.45) * mm, "end": v(-7.86, -34.83) * mm});
            skLineSegment(sketch, "E287", {"start": v(-7.86, -34.83) * mm, "end": v(-8.35, -36.2) * mm});
            skLineSegment(sketch, "E288", {"start": v(-8.35, -36.2) * mm, "end": v(-7.97, -36.2) * mm});
            skLineSegment(sketch, "E289", {"start": v(-7.97, -36.2) * mm, "end": v(-7.83, -36.45) * mm});
            skLineSegment(sketch, "E290", {"start": v(-7.83, -36.45) * mm, "end": v(-8.72, -36.45) * mm});
            skLineSegment(sketch, "E291", {"start": v(-8.03, -34.58) * mm, "end": v(-7.68, -34.58) * mm});
            skLineSegment(sketch, "E292", {"start": v(-6.74, -36.45) * mm, "end": v(-6.74, -34.58) * mm});
            skLineSegment(sketch, "E293", {"start": v(-6.74, -34.58) * mm, "end": v(-6.13, -34.58) * mm});
            skLineSegment(sketch, "E294", {"start": v(-6.13, -34.58) * mm, "end": v(-5.84, -34.87) * mm});
            skLineSegment(sketch, "E295", {"start": v(-5.84, -34.87) * mm, "end": v(-5.84, -35.33) * mm});
            skLineSegment(sketch, "E296", {"start": v(-5.84, -35.33) * mm, "end": v(-6, -35.5) * mm});
            skLineSegment(sketch, "E297", {"start": v(-6, -35.5) * mm, "end": v(-5.84, -36.45) * mm});
            skLineSegment(sketch, "E298", {"start": v(-5.84, -36.45) * mm, "end": v(-6.1, -36.45) * mm});
            skLineSegment(sketch, "E299", {"start": v(-6.1, -36.45) * mm, "end": v(-6.24, -35.62) * mm});
            skLineSegment(sketch, "E300", {"start": v(-6.24, -35.62) * mm, "end": v(-6.5, -35.62) * mm});
            skLineSegment(sketch, "E301", {"start": v(-6.5, -35.62) * mm, "end": v(-6.5, -36.45) * mm});
            skLineSegment(sketch, "E302", {"start": v(-6.5, -36.45) * mm, "end": v(-6.74, -36.45) * mm});
            skLineSegment(sketch, "E303", {"start": v(-6.5, -34.83) * mm, "end": v(-6.5, -35.37) * mm});
            skLineSegment(sketch, "E304", {"start": v(-6.5, -35.37) * mm, "end": v(-6.23, -35.37) * mm});
            skLineSegment(sketch, "E305", {"start": v(-6.23, -35.37) * mm, "end": v(-6.1, -35.23) * mm});
            skLineSegment(sketch, "E306", {"start": v(-6.1, -35.23) * mm, "end": v(-6.1, -34.97) * mm});
            skLineSegment(sketch, "E307", {"start": v(-6.1, -34.97) * mm, "end": v(-6.23, -34.83) * mm});
            skLineSegment(sketch, "E308", {"start": v(-6.23, -34.83) * mm, "end": v(-6.5, -34.83) * mm});
            skLineSegment(sketch, "E309", {"start": v(1.28, -34.58) * mm, "end": v(1.28, -36.45) * mm});
            skLineSegment(sketch, "E310", {"start": v(1.28, -36.45) * mm, "end": v(2.17, -36.45) * mm});
            skLineSegment(sketch, "E311", {"start": v(2.17, -36.45) * mm, "end": v(2.42, -36) * mm});
            skLineSegment(sketch, "E312", {"start": v(2.42, -36) * mm, "end": v(2.42, -35.02) * mm});
            skLineSegment(sketch, "E313", {"start": v(2.42, -35.02) * mm, "end": v(2.17, -34.58) * mm});
            skLineSegment(sketch, "E314", {"start": v(2.17, -34.58) * mm, "end": v(1.28, -34.58) * mm});
            skLineSegment(sketch, "E315", {"start": v(1.53, -34.83) * mm, "end": v(1.53, -36.2) * mm});
            skLineSegment(sketch, "E316", {"start": v(1.53, -36.2) * mm, "end": v(2.02, -36.2) * mm});
            skLineSegment(sketch, "E317", {"start": v(2.02, -36.2) * mm, "end": v(2.17, -35.94) * mm});
            skLineSegment(sketch, "E318", {"start": v(2.17, -35.94) * mm, "end": v(2.17, -35.08) * mm});
            skLineSegment(sketch, "E319", {"start": v(2.17, -35.08) * mm, "end": v(2.02, -34.83) * mm});
            skLineSegment(sketch, "E320", {"start": v(2.02, -34.83) * mm, "end": v(1.53, -34.83) * mm});
            skLineSegment(sketch, "E321", {"start": v(2.68, -36.45) * mm, "end": v(2.68, -34.58) * mm});
            skLineSegment(sketch, "E322", {"start": v(2.68, -34.58) * mm, "end": v(3.3, -34.58) * mm});
            skLineSegment(sketch, "E323", {"start": v(3.3, -34.58) * mm, "end": v(3.59, -34.87) * mm});
            skLineSegment(sketch, "E324", {"start": v(3.59, -34.87) * mm, "end": v(3.59, -35.33) * mm});
            skLineSegment(sketch, "E325", {"start": v(3.59, -35.33) * mm, "end": v(3.42, -35.5) * mm});
            skLineSegment(sketch, "E326", {"start": v(3.42, -35.5) * mm, "end": v(3.59, -36.45) * mm});
            skLineSegment(sketch, "E327", {"start": v(3.59, -36.45) * mm, "end": v(3.33, -36.45) * mm});
            skLineSegment(sketch, "E328", {"start": v(3.33, -36.45) * mm, "end": v(3.19, -35.62) * mm});
            skLineSegment(sketch, "E329", {"start": v(3.19, -35.62) * mm, "end": v(2.93, -35.62) * mm});
            skLineSegment(sketch, "E330", {"start": v(2.93, -35.62) * mm, "end": v(2.93, -36.45) * mm});
            skLineSegment(sketch, "E331", {"start": v(2.93, -36.45) * mm, "end": v(2.68, -36.45) * mm});
            skLineSegment(sketch, "E332", {"start": v(2.93, -34.83) * mm, "end": v(2.93, -35.37) * mm});
            skLineSegment(sketch, "E333", {"start": v(2.93, -35.37) * mm, "end": v(3.19, -35.37) * mm});
            skLineSegment(sketch, "E334", {"start": v(3.19, -35.37) * mm, "end": v(3.33, -35.23) * mm});
            skLineSegment(sketch, "E335", {"start": v(3.33, -35.23) * mm, "end": v(3.33, -34.97) * mm});
            skLineSegment(sketch, "E336", {"start": v(3.33, -34.97) * mm, "end": v(3.19, -34.83) * mm});
            skLineSegment(sketch, "E337", {"start": v(3.19, -34.83) * mm, "end": v(2.93, -34.83) * mm});
            skLineSegment(sketch, "E338", {"start": v(4.1, -34.58) * mm, "end": v(3.84, -34.83) * mm});
            skLineSegment(sketch, "E339", {"start": v(3.84, -34.83) * mm, "end": v(3.84, -36.2) * mm});
            skLineSegment(sketch, "E340", {"start": v(3.84, -36.2) * mm, "end": v(4.1, -36.45) * mm});
            skLineSegment(sketch, "E341", {"start": v(4.1, -36.45) * mm, "end": v(4.6, -36.45) * mm});
            skLineSegment(sketch, "E342", {"start": v(4.6, -36.45) * mm, "end": v(4.86, -36.2) * mm});
            skLineSegment(sketch, "E343", {"start": v(4.86, -36.2) * mm, "end": v(4.86, -34.83) * mm});
            skLineSegment(sketch, "E344", {"start": v(4.86, -34.83) * mm, "end": v(4.6, -34.58) * mm});
            skLineSegment(sketch, "E345", {"start": v(4.6, -34.58) * mm, "end": v(4.1, -34.58) * mm});
            skLineSegment(sketch, "E346", {"start": v(4.1, -34.94) * mm, "end": v(4.1, -36.09) * mm});
            skLineSegment(sketch, "E347", {"start": v(4.1, -36.09) * mm, "end": v(4.2, -36.2) * mm});
            skLineSegment(sketch, "E348", {"start": v(4.2, -36.2) * mm, "end": v(4.5, -36.2) * mm});
            skLineSegment(sketch, "E349", {"start": v(4.5, -36.2) * mm, "end": v(4.6, -36.09) * mm});
            skLineSegment(sketch, "E350", {"start": v(4.6, -36.09) * mm, "end": v(4.6, -34.93) * mm});
            skLineSegment(sketch, "E351", {"start": v(4.6, -34.93) * mm, "end": v(4.5, -34.83) * mm});
            skLineSegment(sketch, "E352", {"start": v(4.5, -34.83) * mm, "end": v(4.2, -34.83) * mm});
            skLineSegment(sketch, "E353", {"start": v(4.2, -34.83) * mm, "end": v(4.1, -34.94) * mm});
            skLineSegment(sketch, "E354", {"start": v(5.1, -34.58) * mm, "end": v(6, -34.58) * mm});
            skLineSegment(sketch, "E355", {"start": v(6, -34.58) * mm, "end": v(5.46, -36.2) * mm});
            skLineSegment(sketch, "E356", {"start": v(5.46, -36.2) * mm, "end": v(6, -36.2) * mm});
            skLineSegment(sketch, "E357", {"start": v(6, -36.2) * mm, "end": v(6, -36.45) * mm});
            skLineSegment(sketch, "E358", {"start": v(6, -36.45) * mm, "end": v(5.1, -36.45) * mm});
            skLineSegment(sketch, "E359", {"start": v(5.1, -36.45) * mm, "end": v(5.65, -34.83) * mm});
            skLineSegment(sketch, "E360", {"start": v(5.65, -34.83) * mm, "end": v(5.1, -34.83) * mm});
            skLineSegment(sketch, "E361", {"start": v(5.1, -34.83) * mm, "end": v(5.1, -34.58) * mm});
            skSolve(sketch);
        }
        {
            var Q0;
            Q0=makeQuery(id+"F8.imprint","IMPRINT",FACE,{"disambiguationData":[TD([[makeQuery(id+"F8.imprint","IMPRINT",EDGE,{"derivedFrom":sQuery(id+"F8.wireOp",EDGE,"E157")}),-1.0]])]});
            var Q1;
            Q1=makeQuery(id+"F8.imprint","IMPRINT",FACE,{"disambiguationData":[TD([[makeQuery(id+"F8.imprint","IMPRINT",EDGE,{"derivedFrom":sQuery(id+"F8.wireOp",EDGE,"E148")}),-1.0]])]});
            var Q2;
            Q2=makeQuery(id+"F8.imprint","IMPRINT",FACE,{"disambiguationData":[TD([[makeQuery(id+"F8.imprint","IMPRINT",EDGE,{"derivedFrom":sQuery(id+"F8.wireOp",EDGE,"E130")}),1.0]])]});
            var Q3;
            Q3=makeQuery(id+"F8.imprint","IMPRINT",FACE,{"disambiguationData":[TD([[makeQuery(id+"F8.imprint","IMPRINT",EDGE,{"derivedFrom":sQuery(id+"F8.wireOp",EDGE,"E165")}),1.0]])]});
            var Q4;
            Q4=makeQuery(id+"F8.imprint","IMPRINT",FACE,{"disambiguationData":[TD([[makeQuery(id+"F8.imprint","IMPRINT",EDGE,{"derivedFrom":sQuery(id+"F8.wireOp",EDGE,"E173")}),1.0]])]});
            var Q5;
            Q5=makeQuery(id+"F8.imprint","IMPRINT",FACE,{"disambiguationData":[TD([[makeQuery(id+"F8.imprint","IMPRINT",EDGE,{"derivedFrom":sQuery(id+"F8.wireOp",EDGE,"E197")}),1.0]])]});
            var Q6;
            Q6=makeQuery(id+"F8.imprint","IMPRINT",FACE,{"disambiguationData":[TD([[makeQuery(id+"F8.imprint","IMPRINT",EDGE,{"derivedFrom":sQuery(id+"F8.wireOp",EDGE,"E203")}),-1.0]])]});
            var Q7;
            Q7=makeQuery(id+"F8.imprint","IMPRINT",FACE,{"disambiguationData":[TD([[makeQuery(id+"F8.imprint","IMPRINT",EDGE,{"derivedFrom":sQuery(id+"F8.wireOp",EDGE,"E218")}),1.0]])]});
            var Q8;
            Q8=makeQuery(id+"F8.imprint","IMPRINT",FACE,{"disambiguationData":[TD([[makeQuery(id+"F8.imprint","IMPRINT",EDGE,{"derivedFrom":sQuery(id+"F8.wireOp",EDGE,"E249")}),1.0]])]});
            var Q9;
            Q9=makeQuery(id+"F8.imprint","IMPRINT",FACE,{"disambiguationData":[TD([[makeQuery(id+"F8.imprint","IMPRINT",EDGE,{"derivedFrom":sQuery(id+"F8.wireOp",EDGE,"E271")}),1.0]])]});
            var Q10;
            Q10=makeQuery(id+"F8.imprint","IMPRINT",FACE,{"disambiguationData":[TD([[makeQuery(id+"F8.imprint","IMPRINT",EDGE,{"derivedFrom":sQuery(id+"F8.wireOp",EDGE,"E283")}),-1.0]])]});
            var Q11;
            Q11=makeQuery(id+"F8.imprint","IMPRINT",FACE,{"disambiguationData":[TD([[makeQuery(id+"F8.imprint","IMPRINT",EDGE,{"derivedFrom":sQuery(id+"F8.wireOp",EDGE,"E292")}),-1.0]])]});
            var Q12;
            Q12=makeQuery(id+"F8.imprint","IMPRINT",FACE,{"disambiguationData":[TD([[makeQuery(id+"F8.imprint","IMPRINT",EDGE,{"derivedFrom":sQuery(id+"F8.wireOp",EDGE,"E309")}),1.0]])]});
            var Q13;
            Q13=makeQuery(id+"F8.imprint","IMPRINT",FACE,{"disambiguationData":[TD([[makeQuery(id+"F8.imprint","IMPRINT",EDGE,{"derivedFrom":sQuery(id+"F8.wireOp",EDGE,"E321")}),-1.0]])]});
            var Q14;
            Q14=makeQuery(id+"F8.imprint","IMPRINT",FACE,{"disambiguationData":[TD([[makeQuery(id+"F8.imprint","IMPRINT",EDGE,{"derivedFrom":sQuery(id+"F8.wireOp",EDGE,"E338")}),1.0]])]});
            var Q15;
            Q15=makeQuery(id+"F8.imprint","IMPRINT",FACE,{"disambiguationData":[TD([[makeQuery(id+"F8.imprint","IMPRINT",EDGE,{"derivedFrom":sQuery(id+"F8.wireOp",EDGE,"E354")}),-1.0]])]});
            var Q16;
            Q16=makeQuery(id+"F8.imprint","IMPRINT",FACE,{"disambiguationData":[TD([[makeQuery(id+"F8.imprint","IMPRINT",EDGE,{"derivedFrom":sQuery(id+"F8.wireOp",EDGE,"E225")}),1.0]])]});
            var Q17;
            Q17=makeQuery(id+"F8.imprint","IMPRINT",FACE,{"disambiguationData":[TD([[makeQuery(id+"F8.imprint","IMPRINT",EDGE,{"derivedFrom":sQuery(id+"F8.wireOp",EDGE,"E229")}),1.0]])]});
            extrude(context, id + "F9", {"entities" : qUnion([Q0, Q1, Q2, Q3, Q4, Q5, Q6, Q7, Q8, Q9, Q10, Q11, Q12, Q13, Q14, Q15, Q16, Q17]), "operationType" : NewBodyOperationType.REMOVE, "oppositeDirection" : true, "depth" : 25.4 * mm, "offsetDistance" : 25.4 * mm});
        }
    });
